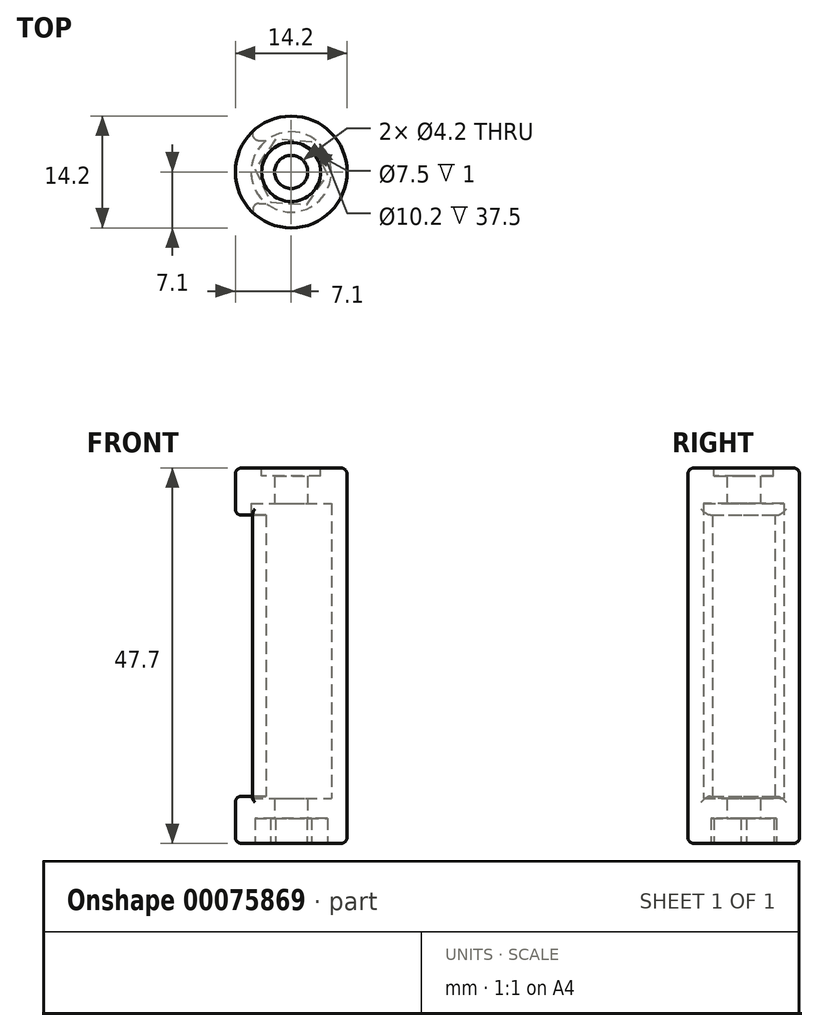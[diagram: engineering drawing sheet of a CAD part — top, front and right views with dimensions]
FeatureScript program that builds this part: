
annotation { "Feature Type Name" : "Feature", "Feature Type Description" : "" }
export const myFeature = defineFeature(function(context is Context, id is Id, definition is map)
    precondition{}
    {
        {
            var Q0;
            Q0=qCreatedBy(makeId("Top.planeOp"),FACE);
            var sketch = newSketch(context, id + "F0", { "sketchPlane" : qUnion([Q0])});
            skCircle(sketch, "E0", {"center": v(0, 0) * mm, "radius": 7.1 * mm});
            skCircle(sketch, "E1", {"center": v(0, 0) * mm, "radius": 2.1 * mm});
            skSolve(sketch);
        }
        {
            var Q0;
            Q0 = qSketchRegion(id + "F0", true);
            extrude(context, id + "F1", {"entities" : qUnion([Q0]), "depth" : 47.7 * mm});
        }
        {
            var Q0;
            Q0=makeQuery(id+"F1.opExtrude","CAP_FACE",FACE,{"disambiguationData":[OSD([sQuery(id+"F0.wireOp",EDGE,"E0"),sQuery(id+"F0.wireOp",EDGE,"E1")])],"isStart":true});
            var sketch = newSketch(context, id + "F2", { "sketchPlane" : qUnion([Q0])});
            skCircle(sketch, "E2.cCircle", {"center": v(0, 0) * mm, "radius": 4 * mm, "construction": true});
            skLineSegment(sketch, "E2.0", {"start": v(4.6, 0.35) * mm, "end": v(2.6, -3.81) * mm});
            skLineSegment(sketch, "E2.1", {"start": v(2.6, -3.81) * mm, "end": v(-2, -4.17) * mm});
            skLineSegment(sketch, "E2.2", {"start": v(-2, -4.17) * mm, "end": v(-4.6, -0.35) * mm});
            skLineSegment(sketch, "E2.3", {"start": v(-4.6, -0.35) * mm, "end": v(-2.6, 3.81) * mm});
            skLineSegment(sketch, "E2.4", {"start": v(-2.6, 3.81) * mm, "end": v(2, 4.17) * mm});
            skLineSegment(sketch, "E2.5", {"start": v(2, 4.17) * mm, "end": v(4.6, 0.35) * mm});
            skPoint(sketch, "E2.0.midPoint", {"position": v(3.6, -1.73) * mm});
            skSolve(sketch);
        }
        {
            var Q0;
            Q0 = qSketchRegion(id + "F2", true);
            extrude(context, id + "F3", {"entities" : qUnion([Q0]), "operationType" : NewBodyOperationType.REMOVE, "oppositeDirection" : true, "depth" : 3.2 * mm});
        }
        {
            var Q0;
            Q0=makeQuery(id+"F1.opExtrude","CAP_FACE",FACE,{"disambiguationData":[OSD([sQuery(id+"F0.wireOp",EDGE,"E0"),sQuery(id+"F0.wireOp",EDGE,"E1")])],"isStart":false});
            var sketch = newSketch(context, id + "F4", { "sketchPlane" : qUnion([Q0])});
            skCircle(sketch, "E3", {"center": v(0, 0) * mm, "radius": 3.75 * mm});
            skSolve(sketch);
        }
        {
            var Q0;
            Q0 = qSketchRegion(id + "F4", true);
            extrude(context, id + "F5", {"entities" : qUnion([Q0]), "operationType" : NewBodyOperationType.REMOVE, "oppositeDirection" : true, "depth" : 1 * mm});
        }
        {
            var Q0;
            Q0=qCreatedBy(makeId("Right.planeOp"),FACE);
            var sketch = newSketch(context, id + "F6", { "sketchPlane" : qUnion([Q0])});
            skLineSegment(sketch, "E4.bottom", {"start": v(-4, 41.7) * mm, "end": v(4, 41.7) * mm});
            skLineSegment(sketch, "E4.top", {"start": v(-4, 6) * mm, "end": v(4, 6) * mm});
            skLineSegment(sketch, "E4.left", {"start": v(-4, 41.7) * mm, "end": v(-4, 6) * mm});
            skLineSegment(sketch, "E4.right", {"start": v(4, 41.7) * mm, "end": v(4, 6) * mm});
            skPoint(sketch, "E4.middle", {"position": v(0, 23.85) * mm});
            skSolve(sketch);
        }
        {
            var Q0;
            Q0 = qSketchRegion(id + "F6", true);
            extrude(context, id + "F7", {"entities" : qUnion([Q0]), "operationType" : NewBodyOperationType.REMOVE, "oppositeDirection" : true, "depth" : 25 * mm});
        }
        {
            var Q0;
            Q0=makeQuery(id+"F3.boolean.opBoolean","COPY",FACE,{"derivedFrom":makeQuery(id+"F3.opExtrude","CAP_FACE",FACE,{"disambiguationData":[OSD([sQuery(id+"F2.wireOp",EDGE,"E2.0"),sQuery(id+"F2.wireOp",EDGE,"E2.1"),sQuery(id+"F2.wireOp",EDGE,"E2.2"),sQuery(id+"F2.wireOp",EDGE,"E2.3"),sQuery(id+"F2.wireOp",EDGE,"E2.4"),sQuery(id+"F2.wireOp",EDGE,"E2.5")])],"isStart":false})});
            var sketch = newSketch(context, id + "F8", { "sketchPlane" : qUnion([Q0])});
            skCircle(sketch, "E5", {"center": v(0, 0) * mm, "radius": 5.1 * mm});
            skSolve(sketch);
        }
        {
            var Q0;
            Q0 = qSketchRegion(id + "F8", true);
            extrude(context, id + "F9", {"entities" : qUnion([Q0]), "operationType" : NewBodyOperationType.REMOVE, "oppositeDirection" : true, "depth" : 40 * mm, "hasSecondDirection" : true, "secondDirectionOppositeDirection" : true, "secondDirectionDepth" : 2.5 * mm});
        }
        {
            var Q0;
            Q0=makeQuery(id+"F1.opExtrude","CAP_EDGE",EDGE,{"disambiguationData":[OSD([sQuery(id+"F0.wireOp",EDGE,"E0")])],"isStart":true});
            var Q1;
            Q1=makeQuery(id+"F7.boolean.opBoolean","INTERSECT",EDGE,{"derivedFrom":[makeQuery(id+"F1.opExtrude","SWEPT_FACE",FACE,{"disambiguationData":[OSD([sQuery(id+"F0.wireOp",EDGE,"E0")])]}),makeQuery(id+"F7.opExtrude","SWEPT_FACE",FACE,{"disambiguationData":[OSD([sQuery(id+"F6.wireOp",EDGE,"E4.top")])]})]});
            var Q2;
            Q2=makeQuery(id+"F7.boolean.opBoolean","INTERSECT",EDGE,{"derivedFrom":[makeQuery(id+"F1.opExtrude","SWEPT_FACE",FACE,{"disambiguationData":[OSD([sQuery(id+"F0.wireOp",EDGE,"E0")])]}),makeQuery(id+"F7.opExtrude","SWEPT_FACE",FACE,{"disambiguationData":[OSD([sQuery(id+"F6.wireOp",EDGE,"E4.bottom")])]})]});
            var Q3;
            Q3=makeQuery(id+"F7.boolean.opBoolean","INTERSECT",EDGE,{"derivedFrom":[makeQuery(id+"F1.opExtrude","SWEPT_FACE",FACE,{"disambiguationData":[OSD([sQuery(id+"F0.wireOp",EDGE,"E0")])]}),makeQuery(id+"F7.opExtrude","SWEPT_FACE",FACE,{"disambiguationData":[OSD([sQuery(id+"F6.wireOp",EDGE,"E4.right")])]})]});
            var Q4;
            Q4=makeQuery(id+"F7.boolean.opBoolean","INTERSECT",EDGE,{"derivedFrom":[makeQuery(id+"F1.opExtrude","SWEPT_FACE",FACE,{"disambiguationData":[OSD([sQuery(id+"F0.wireOp",EDGE,"E0")])]}),makeQuery(id+"F7.opExtrude","SWEPT_FACE",FACE,{"disambiguationData":[OSD([sQuery(id+"F6.wireOp",EDGE,"E4.left")])]})]});
            var Q5;
            Q5=makeQuery(id+"F1.opExtrude","CAP_EDGE",EDGE,{"disambiguationData":[OSD([sQuery(id+"F0.wireOp",EDGE,"E0")])],"isStart":false});
            fillet(context, id + "F10", {"entities" : qUnion([Q0, Q1, Q2, Q3, Q4, Q5]), "radius" : 0.8 * mm, "tangentPropagation" : true, "allowEdgeOverflow" : false});
        }
    });
